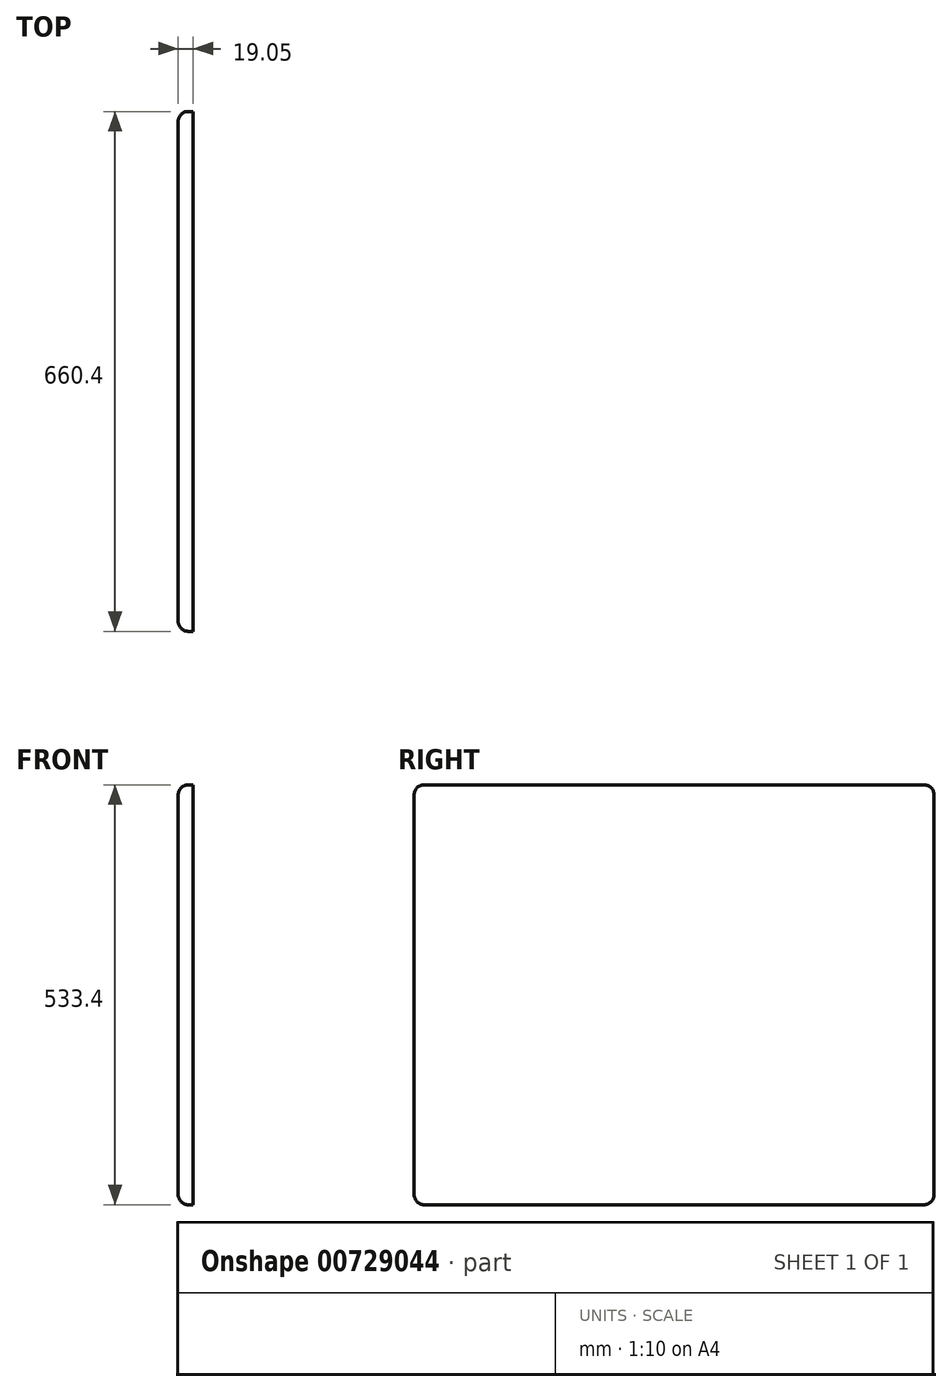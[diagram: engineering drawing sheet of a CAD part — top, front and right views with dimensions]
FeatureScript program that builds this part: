
annotation { "Feature Type Name" : "Feature", "Feature Type Description" : "" }
export const myFeature = defineFeature(function(context is Context, id is Id, definition is map)
    precondition{}
    {
        {
            var Q0;
            Q0=qCreatedBy(makeId("Right.planeOp"),FACE);
            var sketch = newSketch(context, id + "F0", { "sketchPlane" : qUnion([Q0])});
            skLineSegment(sketch, "E0.bottom", {"start": v(-381.06, -265.22) * mm, "end": v(279.34, -265.22) * mm});
            skLineSegment(sketch, "E0.top", {"start": v(-381.06, 268.18) * mm, "end": v(279.34, 268.18) * mm});
            skLineSegment(sketch, "E0.left", {"start": v(-381.06, -265.22) * mm, "end": v(-381.06, 268.18) * mm});
            skLineSegment(sketch, "E0.right", {"start": v(279.34, -265.22) * mm, "end": v(279.34, 268.18) * mm});
            skPoint(sketch, "E0.middle", {"position": v(-50.86, 1.48) * mm});
            skSolve(sketch);
        }
        {
            var Q0;
            Q0 = qSketchRegion(id + "F0", true);
            extrude(context, id + "F1", {"entities" : qUnion([Q0]), "depth" : 19.05 * mm, "offsetDistance" : 25.4 * mm});
        }
        {
            var Q0;
            Q0=makeQuery(id+"F1.opExtrude","CAP_EDGE",EDGE,{"disambiguationData":[OSD([sQuery(id+"F0.wireOp",EDGE,"E0.top")])],"isStart":true});
            var Q1;
            Q1=makeQuery(id+"F1.opExtrude","CAP_EDGE",EDGE,{"disambiguationData":[OSD([sQuery(id+"F0.wireOp",EDGE,"E0.right")])],"isStart":true});
            var Q2;
            Q2=makeQuery(id+"F1.opExtrude","CAP_EDGE",EDGE,{"disambiguationData":[OSD([sQuery(id+"F0.wireOp",EDGE,"E0.left")])],"isStart":true});
            var Q3;
            Q3=makeQuery(id+"F1.opExtrude","CAP_EDGE",EDGE,{"disambiguationData":[OSD([sQuery(id+"F0.wireOp",EDGE,"E0.bottom")])],"isStart":true});
            fillet(context, id + "F2", {"entities" : qUnion([Q0, Q1, Q2, Q3]), "radius" : 12.7 * mm, "tangentPropagation" : true, "allowEdgeOverflow" : false});
        }
        {
            var Q0;
            Q0=makeQuery(id+"F1.opExtrude","SWEPT_EDGE",EDGE,{"disambiguationData":[OSD([sQuery(id+"F0.wireOp",EDGE,"E0.top"),sQuery(id+"F0.wireOp",EDGE,"E0.left")])]});
            var Q1;
            Q1=makeQuery(id+"F2.opFillet","BLEND_EDGE",EDGE,{"blendedFrom":[makeQuery(id+"F1.opExtrude","CAP_EDGE",EDGE,{"disambiguationData":[OSD([sQuery(id+"F0.wireOp",EDGE,"E0.top")])],"isStart":true}),makeQuery(id+"F1.opExtrude","CAP_EDGE",EDGE,{"disambiguationData":[OSD([sQuery(id+"F0.wireOp",EDGE,"E0.left")])],"isStart":true})],"blendedInto":[]});
            fillet(context, id + "F3", {"entities" : qUnion([Q0, Q1]), "radius" : 12.7 * mm, "tangentPropagation" : true, "allowEdgeOverflow" : false});
        }
        {
            var Q0;
            Q0=makeQuery(id+"F1.opExtrude","SWEPT_EDGE",EDGE,{"disambiguationData":[OSD([sQuery(id+"F0.wireOp",EDGE,"E0.top"),sQuery(id+"F0.wireOp",EDGE,"E0.right")])]});
            var Q1;
            Q1=makeQuery(id+"F2.opFillet","BLEND_EDGE",EDGE,{"blendedFrom":[makeQuery(id+"F1.opExtrude","CAP_EDGE",EDGE,{"disambiguationData":[OSD([sQuery(id+"F0.wireOp",EDGE,"E0.top")])],"isStart":true}),makeQuery(id+"F1.opExtrude","CAP_EDGE",EDGE,{"disambiguationData":[OSD([sQuery(id+"F0.wireOp",EDGE,"E0.right")])],"isStart":true})],"blendedInto":[]});
            fillet(context, id + "F4", {"entities" : qUnion([Q0, Q1]), "radius" : 12.7 * mm, "tangentPropagation" : true, "allowEdgeOverflow" : false});
        }
        {
            var Q0;
            Q0=makeQuery(id+"F1.opExtrude","SWEPT_EDGE",EDGE,{"disambiguationData":[OSD([sQuery(id+"F0.wireOp",EDGE,"E0.bottom"),sQuery(id+"F0.wireOp",EDGE,"E0.right")])]});
            var Q1;
            Q1=makeQuery(id+"F2.opFillet","BLEND_EDGE",EDGE,{"blendedFrom":[makeQuery(id+"F1.opExtrude","CAP_EDGE",EDGE,{"disambiguationData":[OSD([sQuery(id+"F0.wireOp",EDGE,"E0.bottom")])],"isStart":true}),makeQuery(id+"F1.opExtrude","CAP_EDGE",EDGE,{"disambiguationData":[OSD([sQuery(id+"F0.wireOp",EDGE,"E0.right")])],"isStart":true})],"blendedInto":[]});
            fillet(context, id + "F5", {"entities" : qUnion([Q0, Q1]), "radius" : 12.7 * mm, "tangentPropagation" : true, "allowEdgeOverflow" : false});
        }
        {
            var Q0;
            Q0=makeQuery(id+"F1.opExtrude","SWEPT_EDGE",EDGE,{"disambiguationData":[OSD([sQuery(id+"F0.wireOp",EDGE,"E0.bottom"),sQuery(id+"F0.wireOp",EDGE,"E0.left")])]});
            var Q1;
            Q1=makeQuery(id+"F2.opFillet","BLEND_EDGE",EDGE,{"blendedFrom":[makeQuery(id+"F1.opExtrude","CAP_EDGE",EDGE,{"disambiguationData":[OSD([sQuery(id+"F0.wireOp",EDGE,"E0.bottom")])],"isStart":true}),makeQuery(id+"F1.opExtrude","CAP_EDGE",EDGE,{"disambiguationData":[OSD([sQuery(id+"F0.wireOp",EDGE,"E0.left")])],"isStart":true})],"blendedInto":[]});
            fillet(context, id + "F6", {"entities" : qUnion([Q0, Q1]), "radius" : 12.7 * mm, "tangentPropagation" : true, "allowEdgeOverflow" : false});
        }
    });
